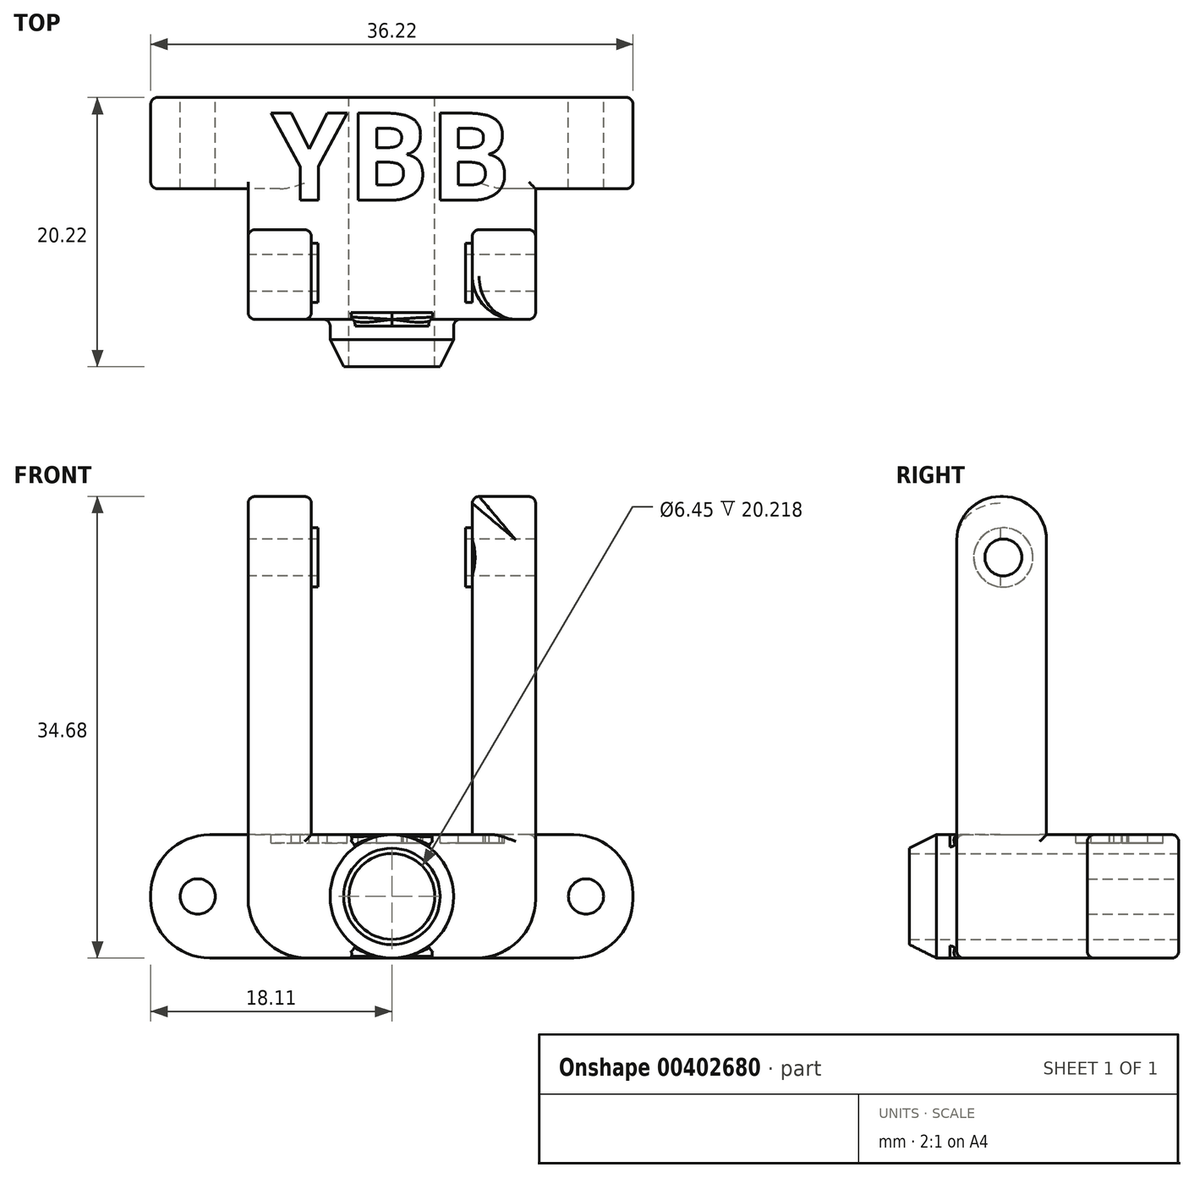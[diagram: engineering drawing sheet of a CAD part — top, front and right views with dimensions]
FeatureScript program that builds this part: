
annotation { "Feature Type Name" : "Feature", "Feature Type Description" : "" }
export const myFeature = defineFeature(function(context is Context, id is Id, definition is map)
    precondition{}
    {
        {
            var Q0;
            Q0=qCreatedBy(makeId("Top.planeOp"),FACE);
            var sketch = newSketch(context, id + "F0", { "sketchPlane" : qUnion([Q0])});
            skLineSegment(sketch, "E0.bottom", {"start": v(10.8, 4.9) * mm, "end": v(-10.8, 4.9) * mm});
            skLineSegment(sketch, "E0.top", {"start": v(10.8, -4.9) * mm, "end": v(-10.8, -4.9) * mm});
            skLineSegment(sketch, "E0.left", {"start": v(10.8, 4.9) * mm, "end": v(10.8, -4.9) * mm});
            skLineSegment(sketch, "E0.right", {"start": v(-10.8, 4.9) * mm, "end": v(-10.8, -4.9) * mm});
            skPoint(sketch, "E0.middle", {"position": v(0, 0) * mm});
            skSolve(sketch);
        }
        {
            var Q0;
            Q0 = qSketchRegion(id + "F0", true);
            extrude(context, id + "F1", {"entities" : qUnion([Q0]), "endBound" : BoundingType.SYMMETRIC, "depth" : 9.27 * mm, "offsetDistance" : 25.4 * mm});
        }
        {
            var Q0;
            Q0=makeQuery(id+"F1.opExtrude","CAP_FACE",FACE,{"disambiguationData":[OSD([sQuery(id+"F0.wireOp",EDGE,"E0.bottom"),sQuery(id+"F0.wireOp",EDGE,"E0.top"),sQuery(id+"F0.wireOp",EDGE,"E0.left"),sQuery(id+"F0.wireOp",EDGE,"E0.right")])],"isStart":false});
            var sketch = newSketch(context, id + "F2", { "sketchPlane" : qUnion([Q0])});
            skLineSegment(sketch, "E1.bottom", {"start": v(-10.8, -4.9) * mm, "end": v(-6.05, -4.9) * mm});
            skLineSegment(sketch, "E1.top", {"start": v(-10.8, 1.83) * mm, "end": v(-6.05, 1.83) * mm});
            skLineSegment(sketch, "E1.left", {"start": v(-10.8, -4.9) * mm, "end": v(-10.8, 1.83) * mm});
            skLineSegment(sketch, "E1.right", {"start": v(-6.05, -4.9) * mm, "end": v(-6.05, 1.83) * mm});
            skLineSegment(sketch, "E2.MirrorCS", {"start": v(10.8, -4.9) * mm, "end": v(10.8, 1.83) * mm});
            skLineSegment(sketch, "E3.MirrorCS", {"start": v(10.8, 1.83) * mm, "end": v(6.05, 1.83) * mm});
            skLineSegment(sketch, "E4.MirrorCS", {"start": v(6.05, -4.9) * mm, "end": v(6.05, 1.83) * mm});
            skLineSegment(sketch, "E5.MirrorCS", {"start": v(10.8, -4.9) * mm, "end": v(6.05, -4.9) * mm});
            skSolve(sketch);
        }
        {
            var Q0;
            Q0 = qSketchRegion(id + "F2", true);
            extrude(context, id + "F3", {"entities" : qUnion([Q0]), "operationType" : NewBodyOperationType.ADD, "depth" : 25.4 * mm, "offsetDistance" : 25.4 * mm});
        }
        {
            var Q0;
            Q0=makeQuery(id+"F1.opExtrude","SWEPT_FACE",FACE,{"disambiguationData":[OSD([sQuery(id+"F0.wireOp",EDGE,"E0.bottom")])]});
            var sketch = newSketch(context, id + "F4", { "sketchPlane" : qUnion([Q0])});
            skLineSegment(sketch, "E6.bottom", {"start": v(-18.11, 4.64) * mm, "end": v(18.11, 4.64) * mm});
            skLineSegment(sketch, "E6.top", {"start": v(-18.11, -4.64) * mm, "end": v(18.11, -4.64) * mm});
            skLineSegment(sketch, "E6.left", {"start": v(-18.11, 4.64) * mm, "end": v(-18.11, -4.64) * mm});
            skLineSegment(sketch, "E6.right", {"start": v(18.11, 4.64) * mm, "end": v(18.11, -4.64) * mm});
            skPoint(sketch, "E6.middle", {"position": v(0, 0) * mm});
            skSolve(sketch);
        }
        {
            var Q0;
            Q0 = qSketchRegion(id + "F4", true);
            extrude(context, id + "F5", {"entities" : qUnion([Q0]), "operationType" : NewBodyOperationType.ADD, "depth" : 6.86 * mm, "offsetDistance" : 25.4 * mm});
        }
        {
            var Q0;
            Q0=makeQuery(id+"F3.boolean.opBoolean","MERGE",FACE,{"derivedFrom":[makeQuery(id+"F1.opExtrude","SWEPT_FACE",FACE,{"disambiguationData":[OSD([sQuery(id+"F0.wireOp",EDGE,"E0.top")])]}),makeQuery(id+"F3.opExtrude","SWEPT_FACE",FACE,{"disambiguationData":[OSD([sQuery(id+"F2.wireOp",EDGE,"E1.bottom")])]}),makeQuery(id+"F3.opExtrude","SWEPT_FACE",FACE,{"disambiguationData":[OSD([sQuery(id+"F2.wireOp",EDGE,"E5.MirrorCS")])]})]});
            var sketch = newSketch(context, id + "F6", { "sketchPlane" : qUnion([Q0])});
            skCircle(sketch, "E7", {"center": v(0, 0) * mm, "radius": 4.64 * mm});
            skSolve(sketch);
        }
        {
            var Q0;
            Q0 = qSketchRegion(id + "F6", true);
            extrude(context, id + "F7", {"entities" : qUnion([Q0]), "operationType" : NewBodyOperationType.ADD, "depth" : 3.56 * mm, "offsetDistance" : 25.4 * mm});
        }
        {
            var Q0;
            Q0=makeQuery(id+"F5.opExtrude","CAP_FACE",FACE,{"disambiguationData":[OSD([sQuery(id+"F4.wireOp",EDGE,"E6.bottom"),sQuery(id+"F4.wireOp",EDGE,"E6.top"),sQuery(id+"F4.wireOp",EDGE,"E6.left"),sQuery(id+"F4.wireOp",EDGE,"E6.right")])],"isStart":false});
            var sketch = newSketch(context, id + "F8", { "sketchPlane" : qUnion([Q0])});
            skCircle(sketch, "E8", {"center": v(14.58, 0) * mm, "radius": 1.32 * mm});
            skCircle(sketch, "E9.MirrorC", {"center": v(-14.58, 0) * mm, "radius": 1.32 * mm});
            skCircle(sketch, "E10", {"center": v(0, 0) * mm, "radius": 3.23 * mm});
            skSolve(sketch);
        }
        {
            var Q0;
            Q0 = qSketchRegion(id + "F8", true);
            extrude(context, id + "F9", {"entities" : qUnion([Q0]), "operationType" : NewBodyOperationType.REMOVE, "endBound" : BoundingType.THROUGH_ALL, "oppositeDirection" : true, "depth" : 25.4 * mm, "offsetDistance" : 25.4 * mm});
        }
        {
            var Q0;
            Q0=makeQuery(id+"F3.boolean.opBoolean","MERGE",FACE,{"derivedFrom":[makeQuery(id+"F1.opExtrude","SWEPT_FACE",FACE,{"disambiguationData":[OSD([sQuery(id+"F0.wireOp",EDGE,"E0.right")])]}),makeQuery(id+"F3.opExtrude","SWEPT_FACE",FACE,{"disambiguationData":[OSD([sQuery(id+"F2.wireOp",EDGE,"E1.left")])]})]});
            var sketch = newSketch(context, id + "F10", { "sketchPlane" : qUnion([Q0])});
            skCircle(sketch, "E11", {"center": v(1.42, 25.46) * mm, "radius": 1.38 * mm});
            skSolve(sketch);
        }
        {
            var Q0;
            Q0 = qSketchRegion(id + "F10", true);
            extrude(context, id + "F11", {"entities" : qUnion([Q0]), "operationType" : NewBodyOperationType.REMOVE, "oppositeDirection" : true, "depth" : 25.4 * mm, "offsetDistance" : 25.4 * mm});
        }
        {
            var Q0;
            Q0=makeQuery(id+"F5.opExtrude","CAP_EDGE",EDGE,{"disambiguationData":[OSD([sQuery(id+"F4.wireOp",EDGE,"E6.top")])],"isStart":false});
            var Q1;
            Q1=makeQuery(id+"F9.boolean.opBoolean","COPY",EDGE,{"derivedFrom":makeQuery(id+"F9.opExtrude","CAP_EDGE",EDGE,{"disambiguationData":[OSD([sQuery(id+"F8.wireOp",EDGE,"E10")])],"isStart":true})});
            var Q2;
            Q2=makeQuery(id+"F5.opExtrude","CAP_EDGE",EDGE,{"disambiguationData":[OSD([sQuery(id+"F4.wireOp",EDGE,"E6.right")])],"isStart":false});
            var Q3;
            Q3=makeQuery(id+"F5.opExtrude","CAP_EDGE",EDGE,{"disambiguationData":[OSD([sQuery(id+"F4.wireOp",EDGE,"E6.bottom")])],"isStart":false});
            var Q4;
            Q4=makeQuery(id+"F3.opExtrude","SWEPT_EDGE",EDGE,{"disambiguationData":[OSD([sQuery(id+"F0.wireOp",EDGE,"E0.right"),sQuery(id+"F2.wireOp",EDGE,"E1.top"),sQuery(id+"F2.wireOp",EDGE,"E1.left")])]});
            var Q5;
            Q5=makeQuery(id+"F3.opExtrude","SWEPT_EDGE",EDGE,{"disambiguationData":[OSD([sQuery(id+"F2.wireOp",EDGE,"E1.top"),sQuery(id+"F2.wireOp",EDGE,"E1.right")])]});
            var Q6;
            Q6=makeQuery(id+"F3.opExtrude","SWEPT_EDGE",EDGE,{"disambiguationData":[OSD([sQuery(id+"F2.wireOp",EDGE,"E3.MirrorCS"),sQuery(id+"F2.wireOp",EDGE,"E4.MirrorCS")])]});
            var Q7;
            Q7=makeQuery(id+"F3.opExtrude","SWEPT_EDGE",EDGE,{"disambiguationData":[OSD([sQuery(id+"F0.wireOp",EDGE,"E0.left"),sQuery(id+"F2.wireOp",EDGE,"E2.MirrorCS"),sQuery(id+"F2.wireOp",EDGE,"E3.MirrorCS")])]});
            var Q8;
            {var subQ1=sQuery(id+"F4.wireOp",EDGE,"E6.top");var subQ2=sQuery(id+"F0.wireOp",EDGE,"E0.left");Q8=makeQuery(id+"F5.boolean.opBoolean","SPLIT",EDGE,{"disambiguationData":[TD([makeQuery(id+"F1.opExtrude","SWEPT_FACE",FACE,{"disambiguationData":[OSD([subQ2])]})])],"derivedFrom":makeQuery(id+"F5.opExtrude","CAP_EDGE",EDGE,{"disambiguationData":[OSD([subQ1])],"isStart":true})});}
            var Q9;
            Q9=makeQuery(id+"F5.opExtrude","CAP_EDGE",EDGE,{"disambiguationData":[OSD([sQuery(id+"F4.wireOp",EDGE,"E6.left")])],"isStart":false});
            var Q10;
            Q10=makeQuery(id+"F5.opExtrude","CAP_EDGE",EDGE,{"disambiguationData":[OSD([sQuery(id+"F4.wireOp",EDGE,"E6.left")])],"isStart":true});
            var Q11;
            {var subQ1=sQuery(id+"F4.wireOp",EDGE,"E6.bottom");var subQ2=sQuery(id+"F0.wireOp",EDGE,"E0.left");Q11=makeQuery(id+"F5.boolean.opBoolean","SPLIT",EDGE,{"disambiguationData":[TD([makeQuery(id+"F1.opExtrude","SWEPT_FACE",FACE,{"disambiguationData":[OSD([subQ2])]})])],"derivedFrom":makeQuery(id+"F5.opExtrude","CAP_EDGE",EDGE,{"disambiguationData":[OSD([subQ1])],"isStart":true})});}
            var Q12;
            Q12=makeQuery(id+"F1.opExtrude","CAP_EDGE",EDGE,{"disambiguationData":[OSD([sQuery(id+"F0.wireOp",EDGE,"E0.left")])],"isStart":false});
            var Q13;
            Q13=makeQuery(id+"F3.opExtrude","CAP_EDGE",EDGE,{"disambiguationData":[OSD([sQuery(id+"F2.wireOp",EDGE,"E3.MirrorCS")])],"isStart":true});
            var Q14;
            Q14=makeQuery(id+"F3.opExtrude","CAP_EDGE",EDGE,{"disambiguationData":[OSD([sQuery(id+"F2.wireOp",EDGE,"E4.MirrorCS")])],"isStart":true});
            var Q15;
            Q15=makeQuery(id+"F3.opExtrude","CAP_EDGE",EDGE,{"disambiguationData":[OSD([sQuery(id+"F2.wireOp",EDGE,"E1.top")])],"isStart":true});
            var Q16;
            {var subQ0=sQuery(id+"F0.wireOp",EDGE,"E0.right");var subQ1=sQuery(id+"F4.wireOp",EDGE,"E6.bottom");Q16=makeQuery(id+"F5.boolean.opBoolean","SPLIT",EDGE,{"disambiguationData":[TD([makeQuery(id+"F1.opExtrude","SWEPT_FACE",FACE,{"disambiguationData":[OSD([subQ0])]})])],"derivedFrom":makeQuery(id+"F5.opExtrude","CAP_EDGE",EDGE,{"disambiguationData":[OSD([subQ1])],"isStart":true})});}
            var Q17;
            {var subQ1=sQuery(id+"F4.wireOp",EDGE,"E6.top");var subQ2=sQuery(id+"F0.wireOp",EDGE,"E0.right");Q17=makeQuery(id+"F5.boolean.opBoolean","SPLIT",EDGE,{"disambiguationData":[TD([makeQuery(id+"F1.opExtrude","SWEPT_FACE",FACE,{"disambiguationData":[OSD([subQ2])]})])],"derivedFrom":makeQuery(id+"F5.opExtrude","CAP_EDGE",EDGE,{"disambiguationData":[OSD([subQ1])],"isStart":true})});}
            var Q18;
            Q18=makeQuery(id+"F5.opExtrude","CAP_EDGE",EDGE,{"disambiguationData":[OSD([sQuery(id+"F4.wireOp",EDGE,"E6.right")])],"isStart":true});
            var Q19;
            Q19=makeQuery(id+"F3.boolean.opBoolean","MERGE",EDGE,{"derivedFrom":[makeQuery(id+"F1.opExtrude","SWEPT_EDGE",EDGE,{"disambiguationData":[OSD([sQuery(id+"F0.wireOp",EDGE,"E0.top"),sQuery(id+"F0.wireOp",EDGE,"E0.right")])]}),makeQuery(id+"F3.opExtrude","SWEPT_EDGE",EDGE,{"disambiguationData":[OSD([sQuery(id+"F2.wireOp",EDGE,"E1.bottom"),sQuery(id+"F2.wireOp",EDGE,"E1.left")])]})]});
            var Q20;
            Q20=makeQuery(id+"F3.boolean.opBoolean","MERGE",EDGE,{"derivedFrom":[makeQuery(id+"F1.opExtrude","SWEPT_EDGE",EDGE,{"disambiguationData":[OSD([sQuery(id+"F0.wireOp",EDGE,"E0.top"),sQuery(id+"F0.wireOp",EDGE,"E0.left")])]}),makeQuery(id+"F3.opExtrude","SWEPT_EDGE",EDGE,{"disambiguationData":[OSD([sQuery(id+"F2.wireOp",EDGE,"E2.MirrorCS"),sQuery(id+"F2.wireOp",EDGE,"E5.MirrorCS")])]})]});
            var Q21;
            Q21=makeQuery(id+"F3.opExtrude","SWEPT_EDGE",EDGE,{"disambiguationData":[OSD([sQuery(id+"F0.wireOp",EDGE,"E0.top"),sQuery(id+"F2.wireOp",EDGE,"E1.bottom"),sQuery(id+"F2.wireOp",EDGE,"E1.right")])]});
            var Q22;
            Q22=makeQuery(id+"F7.boolean.opBoolean","SPLIT",EDGE,{"disambiguationData":[OD(0.0)],"derivedFrom":makeQuery(id+"F7.opExtrude","CAP_EDGE",EDGE,{"disambiguationData":[OSD([sQuery(id+"F6.wireOp",EDGE,"E7")])],"isStart":true})});
            var Q23;
            Q23=makeQuery(id+"F7.boolean.opBoolean","SPLIT",EDGE,{"disambiguationData":[OD(1.0)],"derivedFrom":makeQuery(id+"F7.opExtrude","CAP_EDGE",EDGE,{"disambiguationData":[OSD([sQuery(id+"F6.wireOp",EDGE,"E7")])],"isStart":true})});
            var Q24;
            {var subQ0=sQuery(id+"F0.wireOp",EDGE,"E0.top");Q24=makeQuery(id+"F7.boolean.opBoolean","SPLIT",EDGE,{"disambiguationData":[TD([makeQuery(id+"F3.opExtrude","SWEPT_FACE",FACE,{"disambiguationData":[OSD([sQuery(id+"F2.wireOp",EDGE,"E4.MirrorCS")])]})])],"derivedFrom":makeQuery(id+"F1.opExtrude","CAP_EDGE",EDGE,{"disambiguationData":[OSD([subQ0])],"isStart":false})});}
            var Q25;
            Q25=makeQuery(id+"F3.opExtrude","CAP_EDGE",EDGE,{"disambiguationData":[OSD([sQuery(id+"F2.wireOp",EDGE,"E1.right")])],"isStart":false});
            var Q26;
            Q26=makeQuery(id+"F3.opExtrude","CAP_EDGE",EDGE,{"disambiguationData":[OSD([sQuery(id+"F2.wireOp",EDGE,"E2.MirrorCS")])],"isStart":false});
            var Q27;
            Q27=makeQuery(id+"F3.opExtrude","CAP_EDGE",EDGE,{"disambiguationData":[OSD([sQuery(id+"F2.wireOp",EDGE,"E4.MirrorCS")])],"isStart":false});
            var Q28;
            Q28=makeQuery(id+"F3.opExtrude","CAP_EDGE",EDGE,{"disambiguationData":[OSD([sQuery(id+"F2.wireOp",EDGE,"E1.left")])],"isStart":false});
            var Q29;
            {var subQ0=sQuery(id+"F0.wireOp",EDGE,"E0.left");var subQ1=sQuery(id+"F0.wireOp",EDGE,"E0.top");Q29=makeQuery(id+"F7.boolean.opBoolean","SPLIT",EDGE,{"disambiguationData":[TD([makeQuery(id+"F1.opExtrude","SWEPT_FACE",FACE,{"disambiguationData":[OSD([subQ0])]})])],"derivedFrom":makeQuery(id+"F1.opExtrude","CAP_EDGE",EDGE,{"disambiguationData":[OSD([subQ1])],"isStart":true})});}
            var Q30;
            {var subQ0=sQuery(id+"F0.wireOp",EDGE,"E0.right");var subQ1=sQuery(id+"F0.wireOp",EDGE,"E0.top");Q30=makeQuery(id+"F7.boolean.opBoolean","SPLIT",EDGE,{"disambiguationData":[TD([makeQuery(id+"F1.opExtrude","SWEPT_FACE",FACE,{"disambiguationData":[OSD([subQ0])]})])],"derivedFrom":makeQuery(id+"F1.opExtrude","CAP_EDGE",EDGE,{"disambiguationData":[OSD([subQ1])],"isStart":true})});}
            fillet(context, id + "F12", {"entities" : qUnion([Q0, Q1, Q2, Q3, Q4, Q5, Q6, Q7, Q8, Q9, Q10, Q11, Q12, Q13, Q14, Q15, Q16, Q17, Q18, Q19, Q20, Q21, Q22, Q23, Q24, Q25, Q26, Q27, Q28, Q29, Q30]), "radius" : 0.5 * mm, "tangentPropagation" : true, "allowEdgeOverflow" : false});
        }
        {
            var Q0;
            Q0=makeQuery(id+"F5.opExtrude","SWEPT_EDGE",EDGE,{"disambiguationData":[OSD([sQuery(id+"F4.wireOp",EDGE,"E6.bottom"),sQuery(id+"F4.wireOp",EDGE,"E6.left")])]});
            var Q1;
            Q1=makeQuery(id+"F5.opExtrude","SWEPT_EDGE",EDGE,{"disambiguationData":[OSD([sQuery(id+"F4.wireOp",EDGE,"E6.top"),sQuery(id+"F4.wireOp",EDGE,"E6.left")])]});
            var Q2;
            Q2=makeQuery(id+"F1.opExtrude","CAP_EDGE",EDGE,{"disambiguationData":[OSD([sQuery(id+"F0.wireOp",EDGE,"E0.left")])],"isStart":true});
            var Q3;
            Q3=makeQuery(id+"F1.opExtrude","CAP_EDGE",EDGE,{"disambiguationData":[OSD([sQuery(id+"F0.wireOp",EDGE,"E0.right")])],"isStart":true});
            var Q4;
            Q4=makeQuery(id+"F5.opExtrude","SWEPT_EDGE",EDGE,{"disambiguationData":[OSD([sQuery(id+"F4.wireOp",EDGE,"E6.top"),sQuery(id+"F4.wireOp",EDGE,"E6.right")])]});
            var Q5;
            Q5=makeQuery(id+"F5.opExtrude","SWEPT_EDGE",EDGE,{"disambiguationData":[OSD([sQuery(id+"F4.wireOp",EDGE,"E6.bottom"),sQuery(id+"F4.wireOp",EDGE,"E6.right")])]});
            fillet(context, id + "F13", {"entities" : qUnion([Q0, Q1, Q2, Q3, Q4, Q5]), "radius" : 4.44 * mm, "tangentPropagation" : true, "allowEdgeOverflow" : false});
        }
        {
            var Q0;
            Q0=makeQuery(id+"F3.opExtrude","CAP_EDGE",EDGE,{"disambiguationData":[OSD([sQuery(id+"F2.wireOp",EDGE,"E1.top")])],"isStart":false});
            var Q1;
            Q1=makeQuery(id+"F3.opExtrude","CAP_EDGE",EDGE,{"disambiguationData":[OSD([sQuery(id+"F2.wireOp",EDGE,"E1.bottom")])],"isStart":false});
            var Q2;
            Q2=makeQuery(id+"F3.opExtrude","CAP_EDGE",EDGE,{"disambiguationData":[OSD([sQuery(id+"F2.wireOp",EDGE,"E3.MirrorCS")])],"isStart":false});
            var Q3;
            Q3=makeQuery(id+"F3.opExtrude","CAP_EDGE",EDGE,{"disambiguationData":[OSD([sQuery(id+"F2.wireOp",EDGE,"E5.MirrorCS")])],"isStart":false});
            fillet(context, id + "F14", {"entities" : qUnion([Q0, Q1, Q2, Q3]), "radius" : 3.25 * mm, "tangentPropagation" : true, "allowEdgeOverflow" : false});
        }
        {
            var Q0;
            Q0=makeQuery(id+"F7.opExtrude","CAP_EDGE",EDGE,{"disambiguationData":[OSD([sQuery(id+"F6.wireOp",EDGE,"E7")])],"isStart":false});
            chamfer(context, id + "F15", {"entities" : qUnion([Q0]), "chamferType" : ChamferType.TWO_OFFSETS, "width1" : 1.02 * mm, "oppositeDirection" : false, "width2" : 2.03 * mm, "tangentPropagation" : true});
        }
        {
            var Q0;
            Q0=makeQuery(id+"F3.opExtrude","SWEPT_FACE",FACE,{"disambiguationData":[OSD([sQuery(id+"F2.wireOp",EDGE,"E4.MirrorCS")])]});
            var sketch = newSketch(context, id + "F16", { "sketchPlane" : qUnion([Q0])});
            skCircle(sketch, "E12", {"center": v(1.42, 25.46) * mm, "radius": 2.22 * mm});
            skSolve(sketch);
        }
        {
            var Q0;
            Q0 = qSketchRegion(id + "F16", true);
            extrude(context, id + "F17", {"entities" : qUnion([Q0]), "operationType" : NewBodyOperationType.ADD, "depth" : 0.5 * mm, "offsetDistance" : 25.4 * mm});
        }
        {
            var Q0;
            Q0=makeQuery(id+"F3.opExtrude","SWEPT_FACE",FACE,{"disambiguationData":[OSD([sQuery(id+"F2.wireOp",EDGE,"E1.right")])]});
            var sketch = newSketch(context, id + "F18", { "sketchPlane" : qUnion([Q0])});
            skCircle(sketch, "E13", {"center": v(-1.42, 25.46) * mm, "radius": 2.22 * mm});
            skSolve(sketch);
        }
        {
            var Q0;
            Q0 = qSketchRegion(id + "F18", true);
            extrude(context, id + "F19", {"entities" : qUnion([Q0]), "operationType" : NewBodyOperationType.ADD, "depth" : 0.5 * mm, "offsetDistance" : 25.4 * mm});
        }
        {
            var Q0;
            Q0=makeQuery(id+"F17.opExtrude","CAP_FACE",FACE,{"disambiguationData":[OSD([sQuery(id+"F16.wireOp",EDGE,"E12")])],"isStart":false});
            var sketch = newSketch(context, id + "F20", { "sketchPlane" : qUnion([Q0])});
            skCircle(sketch, "E14", {"center": v(1.42, 25.46) * mm, "radius": 1.38 * mm});
            skSolve(sketch);
        }
        {
            var Q0;
            Q0 = qSketchRegion(id + "F20", true);
            extrude(context, id + "F21", {"entities" : qUnion([Q0]), "operationType" : NewBodyOperationType.REMOVE, "endBound" : BoundingType.SYMMETRIC, "oppositeDirection" : true, "depth" : 25.4 * mm, "offsetDistance" : 25.4 * mm});
        }
        {
            var Q0;
            Q0=makeQuery(id+"F5.boolean.opBoolean","MERGE",FACE,{"derivedFrom":[makeQuery(id+"F1.opExtrude","CAP_FACE",FACE,{"disambiguationData":[OSD([sQuery(id+"F0.wireOp",EDGE,"E0.bottom"),sQuery(id+"F0.wireOp",EDGE,"E0.top"),sQuery(id+"F0.wireOp",EDGE,"E0.left"),sQuery(id+"F0.wireOp",EDGE,"E0.right")])],"isStart":false}),makeQuery(id+"F5.opExtrude","SWEPT_FACE",FACE,{"disambiguationData":[OSD([sQuery(id+"F4.wireOp",EDGE,"E6.bottom")])]})]});
            var sketch = newSketch(context, id + "F22", { "sketchPlane" : qUnion([Q0])});
            skText(sketch, "E15", { "text": "YBB", "fontName": "OpenSans-Bold.ttf"});
            const initialGuessF22  = {"E15": [-0.00906, 0.00405, 1, 0, 0.00659]};
            skSetInitialGuess(sketch, initialGuessF22);
            skSolve(sketch);
        }
        {
            var Q0;
            Q0 = qSketchRegion(id + "F22", true);
            extrude(context, id + "F23", {"entities" : qUnion([Q0]), "operationType" : NewBodyOperationType.REMOVE, "oppositeDirection" : true, "depth" : 0.64 * mm, "offsetDistance" : 25.4 * mm});
        }
    });
